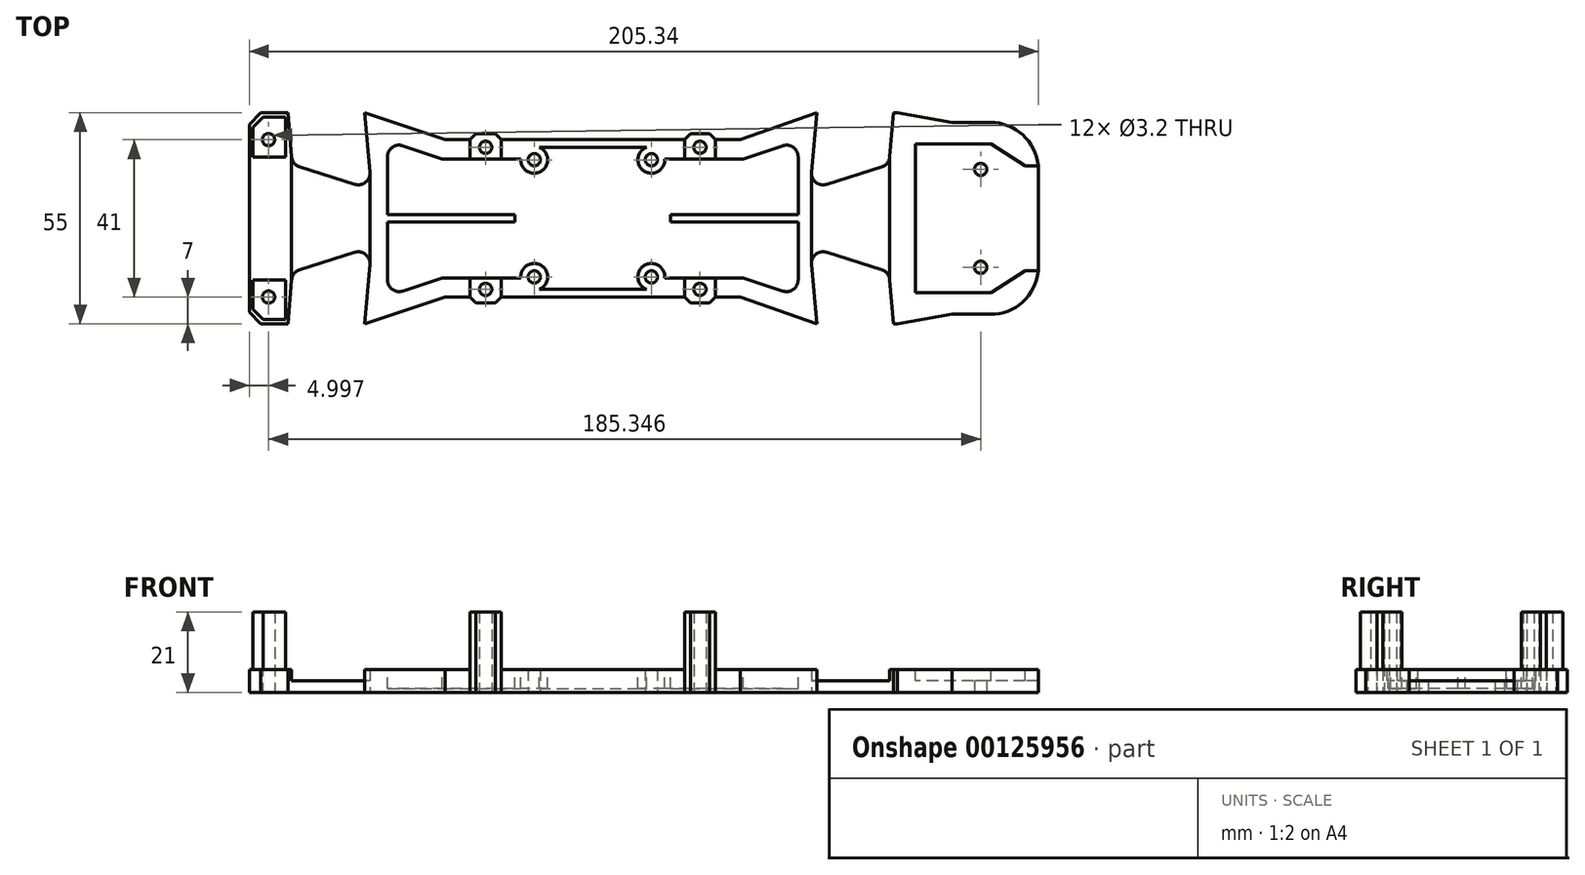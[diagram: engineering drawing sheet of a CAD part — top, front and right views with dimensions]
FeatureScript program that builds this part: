
annotation { "Feature Type Name" : "Feature", "Feature Type Description" : "" }
export const myFeature = defineFeature(function(context is Context, id is Id, definition is map)
    precondition{}
    {
        {
            var Q0;
            Q0=qCreatedBy(makeId("Top.planeOp"),FACE);
            var sketch = newSketch(context, id + "F0", { "sketchPlane" : qUnion([Q0])});
            skLineSegment(sketch, "E0", {"start": v(17.13, -22) * mm, "end": v(18.63, -20.5) * mm});
            skLineSegment(sketch, "E1", {"start": v(66.03, -27.5) * mm, "end": v(80.23, -25) * mm});
            skLineSegment(sketch, "E2", {"start": v(14.63, -22) * mm, "end": v(17.13, -22) * mm});
            skArc(sketch, "E3", {"start": v(90.23, -25) * mm, "mid": v(98.63, -21.75) * mm, "end": v(102.67, -13.7) * mm});
            skLineSegment(sketch, "E4", {"start": v(-102.67, 24.5) * mm, "end": v(-102.67, -24.5) * mm});
            skLineSegment(sketch, "E5", {"start": v(-51.67, -20.5) * mm, "end": v(-45.17, -20.5) * mm});
            skLineSegment(sketch, "E6", {"start": v(12.13, -22) * mm, "end": v(10.63, -20.5) * mm});
            skLineSegment(sketch, "E7", {"start": v(14.63, -22) * mm, "end": v(12.13, -22) * mm});
            skLineSegment(sketch, "E8", {"start": v(-43.67, -22) * mm, "end": v(-38.67, -22) * mm});
            skLineSegment(sketch, "E9", {"start": v(-43.67, -22) * mm, "end": v(-45.17, -20.5) * mm});
            skLineSegment(sketch, "E10", {"start": v(25.13, -20.5) * mm, "end": v(45.03, -27.5) * mm});
            skLineSegment(sketch, "E11", {"start": v(80.23, -25) * mm, "end": v(90.23, -25) * mm});
            skCircle(sketch, "E12", {"center": v(1.98, -15.25) * mm, "radius": 1.6 * mm});
            skCircle(sketch, "E13", {"center": v(-28.52, -15.25) * mm, "radius": 1.6 * mm});
            skLineSegment(sketch, "E14", {"start": v(18.63, -20.5) * mm, "end": v(25.13, -20.5) * mm});
            skCircle(sketch, "E15", {"center": v(87.67, -12.75) * mm, "radius": 1.6 * mm});
            skLineSegment(sketch, "E16", {"start": v(-37.17, -20.5) * mm, "end": v(10.63, -20.5) * mm});
            skLineSegment(sketch, "E17", {"start": v(-72.67, -27.5) * mm, "end": v(-51.67, -20.5) * mm});
            skLineSegment(sketch, "E18", {"start": v(102.67, 13.7) * mm, "end": v(102.67, -13.7) * mm});
            skLineSegment(sketch, "E19", {"start": v(-41.17, -22) * mm, "end": v(-43.67, -22) * mm});
            skLineSegment(sketch, "E20", {"start": v(-38.67, -22) * mm, "end": v(-37.17, -20.5) * mm});
            skLineSegment(sketch, "E21", {"start": v(-99.67, -27.5) * mm, "end": v(-92.67, -27.5) * mm});
            skLineSegment(sketch, "E22", {"start": v(-31.87, 0) * mm, "end": v(-19.1, 0) * mm, "construction": true});
            skLineSegment(sketch, "E23", {"start": v(-13.82, -38.87) * mm, "end": v(-13.82, -45.04) * mm, "construction": true});
            skLineSegment(sketch, "E24", {"start": v(65.02, -27.5) * mm, "end": v(66.03, -27.5) * mm});
            skLineSegment(sketch, "E25.MirrorCS", {"start": v(-43.67, 22) * mm, "end": v(-45.17, 20.5) * mm});
            skLineSegment(sketch, "E26.MirrorCS", {"start": v(-38.67, 22) * mm, "end": v(-37.17, 20.5) * mm});
            skLineSegment(sketch, "E27.MirrorCS", {"start": v(12.13, 22) * mm, "end": v(10.63, 20.5) * mm});
            skLineSegment(sketch, "E28.MirrorCS", {"start": v(14.63, 22) * mm, "end": v(12.13, 22) * mm});
            skLineSegment(sketch, "E29.MirrorCS", {"start": v(65.02, 27.5) * mm, "end": v(66.03, 27.5) * mm});
            skLineSegment(sketch, "E30.MirrorCS", {"start": v(17.13, 22) * mm, "end": v(18.63, 20.5) * mm});
            skLineSegment(sketch, "E31.MirrorCS", {"start": v(14.63, 22) * mm, "end": v(17.13, 22) * mm});
            skLineSegment(sketch, "E32.MirrorCS", {"start": v(-43.67, 22) * mm, "end": v(-38.67, 22) * mm});
            skCircle(sketch, "E33.MirrorC", {"center": v(87.67, 12.75) * mm, "radius": 1.6 * mm});
            skLineSegment(sketch, "E34.MirrorCS", {"start": v(25.13, 20.5) * mm, "end": v(45.03, 27.5) * mm});
            skLineSegment(sketch, "E35.MirrorCS", {"start": v(66.03, 27.5) * mm, "end": v(80.23, 25) * mm});
            skArc(sketch, "E36.MirrorCS", {"start": v(90.23, 25) * mm, "mid": v(98.63, 21.75) * mm, "end": v(102.67, 13.7) * mm});
            skLineSegment(sketch, "E37.MirrorCS", {"start": v(-72.67, 27.5) * mm, "end": v(-51.67, 20.5) * mm});
            skLineSegment(sketch, "E38.MirrorCS", {"start": v(-99.67, 27.5) * mm, "end": v(-92.67, 27.5) * mm});
            skCircle(sketch, "E39.MirrorC", {"center": v(1.98, 15.25) * mm, "radius": 1.6 * mm});
            skLineSegment(sketch, "E40.MirrorCS", {"start": v(-51.67, 20.5) * mm, "end": v(-45.17, 20.5) * mm});
            skCircle(sketch, "E41.MirrorC", {"center": v(-28.52, 15.25) * mm, "radius": 1.6 * mm});
            skLineSegment(sketch, "E42.MirrorCS", {"start": v(-37.17, 20.5) * mm, "end": v(10.63, 20.5) * mm});
            skLineSegment(sketch, "E43.MirrorCS", {"start": v(18.63, 20.5) * mm, "end": v(25.13, 20.5) * mm});
            skLineSegment(sketch, "E44.MirrorCS", {"start": v(80.23, 25) * mm, "end": v(90.23, 25) * mm});
            skCircle(sketch, "E45", {"center": v(-97.67, 20.5) * mm, "radius": 1.6 * mm});
            skCircle(sketch, "E46", {"center": v(-97.67, -20.5) * mm, "radius": 1.6 * mm});
            skLineSegment(sketch, "E47", {"start": v(-99.67, 27.5) * mm, "end": v(-102.67, 24.5) * mm});
            skLineSegment(sketch, "E48", {"start": v(-99.67, -27.5) * mm, "end": v(-102.67, -24.5) * mm});
            skLineSegment(sketch, "E49", {"start": v(-92.67, -27.5) * mm, "end": v(-91.67, -16) * mm});
            skLineSegment(sketch, "E50", {"start": v(-72.67, -27.5) * mm, "end": v(-71.31, -11.98) * mm});
            skLineSegment(sketch, "E51", {"start": v(-89.58, -13.4) * mm, "end": v(-75.2, -8.85) * mm});
            skPoint(sketch, "E52.visualSharp", {"position": v(-91.5, -14) * mm});
            skArc(sketch, "E52.filletArc", {"start": v(-89.58, -13.4) * mm, "mid": v(-91.02, -14.38) * mm, "end": v(-91.67, -16) * mm});
            skPoint(sketch, "E53.visualSharp", {"position": v(-70.92, -7.5) * mm});
            skArc(sketch, "E53.filletArc", {"start": v(-71.31, -11.98) * mm, "mid": v(-72.43, -9.37) * mm, "end": v(-75.2, -8.85) * mm});
            skLineSegment(sketch, "E54.MirrorCS", {"start": v(65.02, -27.5) * mm, "end": v(64.02, -16) * mm});
            skArc(sketch, "E55.MirrorCS", {"start": v(61.93, -13.4) * mm, "mid": v(63.37, -14.38) * mm, "end": v(64.02, -16) * mm});
            skLineSegment(sketch, "E56.MirrorCS", {"start": v(61.93, -13.4) * mm, "end": v(47.56, -8.85) * mm});
            skArc(sketch, "E57.MirrorCS", {"start": v(43.67, -11.98) * mm, "mid": v(44.78, -9.37) * mm, "end": v(47.56, -8.85) * mm});
            skLineSegment(sketch, "E58.MirrorCS", {"start": v(45.02, -27.5) * mm, "end": v(43.67, -11.98) * mm});
            skLineSegment(sketch, "E59.MirrorCS", {"start": v(-92.67, 27.5) * mm, "end": v(-91.67, 16) * mm});
            skPoint(sketch, "E60.MirrorP", {"position": v(-91.5, 14) * mm});
            skArc(sketch, "E61.MirrorCS", {"start": v(-89.58, 13.4) * mm, "mid": v(-91.02, 14.38) * mm, "end": v(-91.67, 16) * mm});
            skLineSegment(sketch, "E62.MirrorCS", {"start": v(-89.58, 13.4) * mm, "end": v(-75.2, 8.85) * mm});
            skArc(sketch, "E63.MirrorCS", {"start": v(-71.31, 11.98) * mm, "mid": v(-72.43, 9.37) * mm, "end": v(-75.2, 8.85) * mm});
            skLineSegment(sketch, "E64.MirrorCS", {"start": v(-72.67, 27.5) * mm, "end": v(-71.31, 11.98) * mm});
            skLineSegment(sketch, "E65.MirrorCS", {"start": v(65.02, 27.5) * mm, "end": v(64.02, 16) * mm});
            skArc(sketch, "E66.MirrorCS", {"start": v(61.93, 13.4) * mm, "mid": v(63.37, 14.38) * mm, "end": v(64.02, 16) * mm});
            skLineSegment(sketch, "E67.MirrorCS", {"start": v(61.93, 13.4) * mm, "end": v(47.56, 8.85) * mm});
            skArc(sketch, "E68.MirrorCS", {"start": v(43.67, 11.98) * mm, "mid": v(44.78, 9.37) * mm, "end": v(47.56, 8.85) * mm});
            skLineSegment(sketch, "E69.MirrorCS", {"start": v(45.02, 27.5) * mm, "end": v(43.67, 11.98) * mm});
            skCircle(sketch, "E70", {"center": v(-41.17, 18.5) * mm, "radius": 1.6 * mm});
            skCircle(sketch, "E71.MirrorC", {"center": v(-41.17, -18.5) * mm, "radius": 1.6 * mm});
            skLineSegment(sketch, "E72", {"start": v(-13.27, -11.98) * mm, "end": v(-13.27, -8.87) * mm, "construction": true});
            skCircle(sketch, "E73.MirrorC", {"center": v(14.63, -18.5) * mm, "radius": 1.6 * mm});
            skCircle(sketch, "E74.MirrorC", {"center": v(14.63, 18.5) * mm, "radius": 1.6 * mm});
            skSolve(sketch);
        }
        {
            var Q0;
            Q0=makeQuery(id+"F0.imprint","IMPRINT",FACE,{"disambiguationData":[TD([[makeQuery(id+"F0.imprint","IMPRINT",EDGE,{"derivedFrom":sQuery(id+"F0.wireOp",EDGE,"E0")}),1.0]])]});
            extrude(context, id + "F1", {"entities" : qUnion([Q0]), "depth" : 3 * mm});
        }
        {
            var Q0;
            Q0=makeQuery(id+"F1.opExtrude","CAP_FACE",FACE,{"disambiguationData":[OSD([sQuery(id+"F0.wireOp",EDGE,"E0"),sQuery(id+"F0.wireOp",EDGE,"E1"),sQuery(id+"F0.wireOp",EDGE,"E2"),sQuery(id+"F0.wireOp",EDGE,"E3"),sQuery(id+"F0.wireOp",EDGE,"E4"),sQuery(id+"F0.wireOp",EDGE,"E5"),sQuery(id+"F0.wireOp",EDGE,"E6"),sQuery(id+"F0.wireOp",EDGE,"E7"),sQuery(id+"F0.wireOp",EDGE,"E8"),sQuery(id+"F0.wireOp",EDGE,"E9"),sQuery(id+"F0.wireOp",EDGE,"E10"),sQuery(id+"F0.wireOp",EDGE,"E11"),sQuery(id+"F0.wireOp",EDGE,"E12"),sQuery(id+"F0.wireOp",EDGE,"E13"),sQuery(id+"F0.wireOp",EDGE,"E14"),sQuery(id+"F0.wireOp",EDGE,"E15"),sQuery(id+"F0.wireOp",EDGE,"E16"),sQuery(id+"F0.wireOp",EDGE,"E17"),sQuery(id+"F0.wireOp",EDGE,"E18"),sQuery(id+"F0.wireOp",EDGE,"E19"),sQuery(id+"F0.wireOp",EDGE,"cacf1cef-0e85-476d-93d9-f38397325373"),sQuery(id+"F0.wireOp",EDGE,"E20"),sQuery(id+"F0.wireOp",EDGE,"E21"),sQuery(id+"F0.wireOp",EDGE,"ktilFzmr-dvzl-N5Si-9QJE-yYhrjEpCdq7n"),sQuery(id+"F0.wireOp",EDGE,"E24"),sQuery(id+"F0.wireOp",EDGE,"y4Y6HD6z-qHML-mSbB-IgaJ-mIwfbL7wUbv0"),sQuery(id+"F0.wireOp",EDGE,"iBA37CV8-DKIr-jiMQ-xKjg-X3JWPwUv4cM2"),sQuery(id+"F0.wireOp",EDGE,"d3470dd5-383c-460f-b080-c6315553abd8.filletArc"),sQuery(id+"F0.wireOp",EDGE,"3242f57e-5447-41c4-bb9e-3e6edaabaf53.filletArc"),sQuery(id+"F0.wireOp",EDGE,"8b0b9065-8131-4a12-877d-2f3f4031bb290.MirrorCS"),sQuery(id+"F0.wireOp",EDGE,"cd60102b-e517-490f-9958-59f3726d56970.MirrorCS"),sQuery(id+"F0.wireOp",EDGE,"a92283b3-0195-4067-93ac-9b1154ab97d00.MirrorCS"),sQuery(id+"F0.wireOp",EDGE,"be52c130-8e04-43e8-8735-bc38e122cce20.MirrorCS"),sQuery(id+"F0.wireOp",EDGE,"8f306e8a-6cf5-47b0-af38-d5a049e91b220.MirrorCS"),sQuery(id+"F0.wireOp",EDGE,"E25.MirrorCS"),sQuery(id+"F0.wireOp",EDGE,"E26.MirrorCS"),sQuery(id+"F0.wireOp",EDGE,"E27.MirrorCS"),sQuery(id+"F0.wireOp",EDGE,"E28.MirrorCS"),sQuery(id+"F0.wireOp",EDGE,"E29.MirrorCS"),sQuery(id+"F0.wireOp",EDGE,"0e7726c4-7c47-45c0-a996-f9083ab80f9b5.MirrorCS"),sQuery(id+"F0.wireOp",EDGE,"E30.MirrorCS"),sQuery(id+"F0.wireOp",EDGE,"E31.MirrorCS"),sQuery(id+"F0.wireOp",EDGE,"E32.MirrorCS"),sQuery(id+"F0.wireOp",EDGE,"0e7726c4-7c47-45c0-a996-f9083ab80f9b9.MirrorCS"),sQuery(id+"F0.wireOp",EDGE,"E260.MirrorCS"),sQuery(id+"F0.wireOp",EDGE,"E33.MirrorC"),sQuery(id+"F0.wireOp",EDGE,"E262.MirrorCS"),sQuery(id+"F0.wireOp",EDGE,"E263.MirrorCS"),sQuery(id+"F0.wireOp",EDGE,"E34.MirrorCS"),sQuery(id+"F0.wireOp",EDGE,"E265.MirrorCS"),sQuery(id+"F0.wireOp",EDGE,"E266.MirrorCS"),sQuery(id+"F0.wireOp",EDGE,"E35.MirrorCS"),sQuery(id+"F0.wireOp",EDGE,"E36.MirrorCS"),sQuery(id+"F0.wireOp",EDGE,"E37.MirrorCS"),sQuery(id+"F0.wireOp",EDGE,"E270.MirrorCS"),sQuery(id+"F0.wireOp",EDGE,"E271.MirrorCS"),sQuery(id+"F0.wireOp",EDGE,"E273.MirrorCS"),sQuery(id+"F0.wireOp",EDGE,"E38.MirrorCS"),sQuery(id+"F0.wireOp",EDGE,"E39.MirrorC"),sQuery(id+"F0.wireOp",EDGE,"E40.MirrorCS"),sQuery(id+"F0.wireOp",EDGE,"E278.MirrorCS"),sQuery(id+"F0.wireOp",EDGE,"E41.MirrorC"),sQuery(id+"F0.wireOp",EDGE,"E280.MirrorCS"),sQuery(id+"F0.wireOp",EDGE,"E42.MirrorCS"),sQuery(id+"F0.wireOp",EDGE,"E43.MirrorCS"),sQuery(id+"F0.wireOp",EDGE,"E44.MirrorCS")])],"isStart":false});
            var sketch = newSketch(context, id + "F2", { "sketchPlane" : qUnion([Q0])});
            skLineSegment(sketch, "E75", {"start": v(-91.67, 16.06) * mm, "end": v(-91.67, -16.06) * mm});
            skLineSegment(sketch, "E76", {"start": v(64.02, 16.06) * mm, "end": v(64.02, -16.06) * mm});
            skLineSegment(sketch, "E77", {"start": v(-71.31, 11.98) * mm, "end": v(-71.31, -11.98) * mm});
            skLineSegment(sketch, "E78", {"start": v(43.67, 11.98) * mm, "end": v(43.67, -11.98) * mm});
            skSolve(sketch);
        }
        {
            var Q0;
            {var subQ3=sQuery(id+"F2.wireOp",EDGE,"E75");Q0=makeQuery(id+"F2.imprint","IMPRINT",FACE,{"disambiguationData":[TD([[makeQuery(id+"F2.imprint","IMPRINT",EDGE,{"derivedFrom":subQ3}),-1.0]])]});}
            var Q1;
            Q1=makeQuery(id+"F2.imprint","IMPRINT",FACE,{"disambiguationData":[TD([[makeQuery(id+"F2.imprint","IMPRINT",EDGE,{"derivedFrom":makeQuery(id+"F1.opExtrude","CAP_EDGE",EDGE,{"disambiguationData":[OSD([sQuery(id+"F0.wireOp",EDGE,"E0")])],"isStart":false})}),1.0]])]});
            var Q2;
            {var subQ1=sQuery(id+"F2.wireOp",EDGE,"E76");Q2=makeQuery(id+"F2.imprint","IMPRINT",FACE,{"disambiguationData":[TD([[makeQuery(id+"F2.imprint","IMPRINT",EDGE,{"derivedFrom":subQ1}),1.0]])]});}
            extrude(context, id + "F3", {"entities" : qUnion([Q0, Q1, Q2]), "operationType" : NewBodyOperationType.ADD, "depth" : 3 * mm});
        }
        {
            var Q0;
            Q0=makeQuery(id+"F3.opExtrude","CAP_FACE",FACE,{"disambiguationData":[OSD([sQuery(id+"F0.wireOp",EDGE,"E0"),sQuery(id+"F0.wireOp",EDGE,"E2"),sQuery(id+"F0.wireOp",EDGE,"E5"),sQuery(id+"F0.wireOp",EDGE,"E6"),sQuery(id+"F0.wireOp",EDGE,"E7"),sQuery(id+"F0.wireOp",EDGE,"E8"),sQuery(id+"F0.wireOp",EDGE,"E9"),sQuery(id+"F0.wireOp",EDGE,"E10"),sQuery(id+"F0.wireOp",EDGE,"E12"),sQuery(id+"F0.wireOp",EDGE,"E13"),sQuery(id+"F0.wireOp",EDGE,"E14"),sQuery(id+"F0.wireOp",EDGE,"E16"),sQuery(id+"F0.wireOp",EDGE,"E17"),sQuery(id+"F0.wireOp",EDGE,"E19"),sQuery(id+"F0.wireOp",EDGE,"E20"),sQuery(id+"F0.wireOp",EDGE,"E25.MirrorCS"),sQuery(id+"F0.wireOp",EDGE,"E26.MirrorCS"),sQuery(id+"F0.wireOp",EDGE,"E27.MirrorCS"),sQuery(id+"F0.wireOp",EDGE,"E28.MirrorCS"),sQuery(id+"F0.wireOp",EDGE,"E30.MirrorCS"),sQuery(id+"F0.wireOp",EDGE,"E31.MirrorCS"),sQuery(id+"F0.wireOp",EDGE,"E32.MirrorCS"),sQuery(id+"F0.wireOp",EDGE,"0e7726c4-7c47-45c0-a996-f9083ab80f9b9.MirrorCS"),sQuery(id+"F0.wireOp",EDGE,"E34.MirrorCS"),sQuery(id+"F0.wireOp",EDGE,"E37.MirrorCS"),sQuery(id+"F0.wireOp",EDGE,"E39.MirrorC"),sQuery(id+"F0.wireOp",EDGE,"E40.MirrorCS"),sQuery(id+"F0.wireOp",EDGE,"E41.MirrorC"),sQuery(id+"F0.wireOp",EDGE,"E42.MirrorCS"),sQuery(id+"F0.wireOp",EDGE,"E43.MirrorCS"),sQuery(id+"F2.wireOp",EDGE,"XH4723qV-k9EK-rnyf-MCnd-NPgPMgAZq0qj"),sQuery(id+"F2.wireOp",EDGE,"VkoqZiKv-uEe6-g3Ky-yl9S-WlclnUHpSLVB"),sQuery(id+"F2.wireOp",EDGE,"4zoe9t7i-jXsD-BC2V-jVCx-dnIx5Sm0L1ok"),sQuery(id+"F2.wireOp",EDGE,"oUknClw5-JEGL-fXPA-mKYg-SWGIKpQydZco"),sQuery(id+"F2.wireOp",EDGE,"MJO4RlAT-fQuh-MutT-Yoxh-jH0xN2Fm8YoV"),sQuery(id+"F2.wireOp",EDGE,"r3oGAgAb-fgCM-ykX4-cEjS-qaDw403mrGcw")])],"isStart":false});
            var sketch = newSketch(context, id + "F4", { "sketchPlane" : qUnion([Q0])});
            skLineSegment(sketch, "E79", {"start": v(-62.77, 18.93) * mm, "end": v(-52.48, 15.5) * mm});
            skLineSegment(sketch, "E80", {"start": v(-52.48, 15.5) * mm, "end": v(-32.01, 15.5) * mm});
            skCircle(sketch, "E81", {"center": v(-28.52, 15.25) * mm, "radius": 3.5 * mm, "construction": true});
            skLineSegment(sketch, "E82", {"start": v(-8.2, 0) * mm, "end": v(-15.48, 0) * mm, "construction": true});
            skLineSegment(sketch, "E83", {"start": v(-13.27, -7.12) * mm, "end": v(-13.27, -2.95) * mm, "construction": true});
            skCircle(sketch, "E84", {"center": v(1.98, 15.25) * mm, "radius": 3.5 * mm, "construction": true});
            skLineSegment(sketch, "E85", {"start": v(-27.22, 18.5) * mm, "end": v(0.68, 18.5) * mm});
            skLineSegment(sketch, "E86.MirrorCS", {"start": v(25.94, 15.5) * mm, "end": v(5.47, 15.5) * mm});
            skLineSegment(sketch, "E87.MirrorCS", {"start": v(36.22, 18.93) * mm, "end": v(25.94, 15.5) * mm});
            skLineSegment(sketch, "E88.MirrorCS", {"start": v(-52.48, -15.5) * mm, "end": v(-32.01, -15.5) * mm});
            skLineSegment(sketch, "E89.MirrorCS", {"start": v(-62.77, -18.93) * mm, "end": v(-52.48, -15.5) * mm});
            skCircle(sketch, "E90.MirrorC", {"center": v(1.98, -15.25) * mm, "radius": 3.5 * mm, "construction": true});
            skCircle(sketch, "E91.MirrorC", {"center": v(-28.52, -15.25) * mm, "radius": 3.5 * mm, "construction": true});
            skLineSegment(sketch, "E92.MirrorCS", {"start": v(-27.22, -18.5) * mm, "end": v(0.68, -18.5) * mm});
            skLineSegment(sketch, "E93.MirrorCS", {"start": v(36.22, -18.93) * mm, "end": v(25.94, -15.5) * mm});
            skLineSegment(sketch, "E94.MirrorCS", {"start": v(25.94, -15.5) * mm, "end": v(5.47, -15.5) * mm});
            skLineSegment(sketch, "E95", {"start": v(-66.71, 16.08) * mm, "end": v(-66.71, -16.08) * mm});
            skLineSegment(sketch, "E96", {"start": v(40.17, 16.08) * mm, "end": v(40.17, -16.08) * mm});
            skPoint(sketch, "E97.visualSharp", {"position": v(-66.71, 20.24) * mm});
            skArc(sketch, "E97.filletArc", {"start": v(-62.77, 18.93) * mm, "mid": v(-65.47, 18.51) * mm, "end": v(-66.71, 16.08) * mm});
            skPoint(sketch, "E98.visualSharp", {"position": v(-66.71, -20.24) * mm});
            skArc(sketch, "E98.filletArc", {"start": v(-66.71, -16.08) * mm, "mid": v(-65.47, -18.51) * mm, "end": v(-62.77, -18.93) * mm});
            skPoint(sketch, "E99.visualSharp", {"position": v(40.17, 20.24) * mm});
            skArc(sketch, "E99.filletArc", {"start": v(40.17, 16.08) * mm, "mid": v(38.92, 18.51) * mm, "end": v(36.22, 18.93) * mm});
            skPoint(sketch, "E100.visualSharp", {"position": v(40.17, -20.24) * mm});
            skArc(sketch, "E100.filletArc", {"start": v(36.22, -18.93) * mm, "mid": v(38.92, -18.51) * mm, "end": v(40.17, -16.08) * mm});
            skLineSegment(sketch, "E101", {"start": v(-33.52, 1) * mm, "end": v(-66.71, 1) * mm});
            skLineSegment(sketch, "E102.MirrorCS", {"start": v(6.98, 1) * mm, "end": v(40.17, 1) * mm});
            skLineSegment(sketch, "E103.MirrorCS", {"start": v(-33.52, -1) * mm, "end": v(-66.71, -1) * mm});
            skLineSegment(sketch, "E104.MirrorCS", {"start": v(6.98, -1) * mm, "end": v(40.17, -1) * mm});
            skLineSegment(sketch, "E105", {"start": v(-33.52, 1) * mm, "end": v(-33.52, -1) * mm});
            skLineSegment(sketch, "E106", {"start": v(6.98, 1) * mm, "end": v(6.98, -1) * mm});
            skArc(sketch, "E107", {"start": v(-32.01, -15.5) * mm, "mid": v(-26.67, -12.28) * mm, "end": v(-27.22, -18.5) * mm});
            skArc(sketch, "E108", {"start": v(0.68, -18.5) * mm, "mid": v(0.12, -12.28) * mm, "end": v(5.47, -15.5) * mm});
            skArc(sketch, "E109", {"start": v(5.47, 15.5) * mm, "mid": v(0.12, 12.28) * mm, "end": v(0.68, 18.5) * mm});
            skArc(sketch, "E110", {"start": v(-32.01, 15.5) * mm, "mid": v(-26.67, 12.28) * mm, "end": v(-27.22, 18.5) * mm});
            skSolve(sketch);
        }
        {
            var Q0;
            Q0=makeQuery(id+"F4.imprint","IMPRINT",FACE,{"disambiguationData":[TD([[makeQuery(id+"F4.imprint","IMPRINT",EDGE,{"derivedFrom":sQuery(id+"F4.wireOp",EDGE,"E79")}),-1.0]])]});
            extrude(context, id + "F5", {"entities" : qUnion([Q0]), "operationType" : NewBodyOperationType.REMOVE, "oppositeDirection" : true, "depth" : 5 * mm});
        }
        {
            var Q0;
            Q0=makeQuery(id+"F3.opExtrude","CAP_FACE",FACE,{"disambiguationData":[OSD([sQuery(id+"F0.wireOp",EDGE,"E4"),sQuery(id+"F0.wireOp",EDGE,"E21"),sQuery(id+"F0.wireOp",EDGE,"ktilFzmr-dvzl-N5Si-9QJE-yYhrjEpCdq7n"),sQuery(id+"F0.wireOp",EDGE,"E38.MirrorCS"),sQuery(id+"F0.wireOp",EDGE,"E280.MirrorCS"),sQuery(id+"F0.wireOp",EDGE,"E45"),sQuery(id+"F0.wireOp",EDGE,"E46"),sQuery(id+"F0.wireOp",EDGE,"E47"),sQuery(id+"F0.wireOp",EDGE,"E48"),sQuery(id+"F2.wireOp",EDGE,"E75")])],"isStart":false});
            var sketch = newSketch(context, id + "F6", { "sketchPlane" : qUnion([Q0])});
            skLineSegment(sketch, "E111", {"start": v(-93.19, -26.38) * mm, "end": v(-99.14, -26.38) * mm});
            skLineSegment(sketch, "E112", {"start": v(-99.14, -26.38) * mm, "end": v(-101.78, -23.73) * mm});
            skLineSegment(sketch, "E113", {"start": v(-101.78, -23.73) * mm, "end": v(-101.78, -16.01) * mm});
            skLineSegment(sketch, "E114", {"start": v(-101.78, -16.01) * mm, "end": v(-93.19, -16.01) * mm});
            skLineSegment(sketch, "E115", {"start": v(-93.19, -16.01) * mm, "end": v(-93.19, -26.38) * mm});
            skLineSegment(sketch, "E116", {"start": v(-94.05, 0) * mm, "end": v(-99.2, 0) * mm, "construction": true});
            skLineSegment(sketch, "E117.MirrorCS", {"start": v(-93.19, 16.01) * mm, "end": v(-93.19, 26.38) * mm});
            skLineSegment(sketch, "E118.MirrorCS", {"start": v(-101.78, 16.01) * mm, "end": v(-93.19, 16.01) * mm});
            skLineSegment(sketch, "E119.MirrorCS", {"start": v(-101.78, 23.73) * mm, "end": v(-101.78, 16.01) * mm});
            skLineSegment(sketch, "E120.MirrorCS", {"start": v(-99.14, 26.38) * mm, "end": v(-101.78, 23.73) * mm});
            skLineSegment(sketch, "E121.MirrorCS", {"start": v(-93.19, 26.38) * mm, "end": v(-99.14, 26.38) * mm});
            skSolve(sketch);
        }
        {
            var Q0;
            Q0=makeQuery(id+"F6.imprint","IMPRINT",FACE,{"disambiguationData":[TD([[makeQuery(id+"F6.imprint","IMPRINT",EDGE,{"derivedFrom":sQuery(id+"F6.wireOp",EDGE,"E117.MirrorCS")}),1.0]])]});
            var Q1;
            Q1=makeQuery(id+"F6.imprint","IMPRINT",FACE,{"disambiguationData":[TD([[makeQuery(id+"F6.imprint","IMPRINT",EDGE,{"derivedFrom":sQuery(id+"F6.wireOp",EDGE,"E111")}),-1.0]])]});
            extrude(context, id + "F7", {"entities" : qUnion([Q0, Q1]), "operationType" : NewBodyOperationType.ADD, "depth" : 15 * mm});
        }
        {
            var Q0;
            Q0=makeQuery(id+"F3.opExtrude","CAP_FACE",FACE,{"disambiguationData":[OSD([sQuery(id+"F0.wireOp",EDGE,"E0"),sQuery(id+"F0.wireOp",EDGE,"E2"),sQuery(id+"F0.wireOp",EDGE,"E5"),sQuery(id+"F0.wireOp",EDGE,"E6"),sQuery(id+"F0.wireOp",EDGE,"E7"),sQuery(id+"F0.wireOp",EDGE,"E8"),sQuery(id+"F0.wireOp",EDGE,"E9"),sQuery(id+"F0.wireOp",EDGE,"E10"),sQuery(id+"F0.wireOp",EDGE,"E12"),sQuery(id+"F0.wireOp",EDGE,"E13"),sQuery(id+"F0.wireOp",EDGE,"E14"),sQuery(id+"F0.wireOp",EDGE,"E16"),sQuery(id+"F0.wireOp",EDGE,"E17"),sQuery(id+"F0.wireOp",EDGE,"E19"),sQuery(id+"F0.wireOp",EDGE,"E20"),sQuery(id+"F0.wireOp",EDGE,"E25.MirrorCS"),sQuery(id+"F0.wireOp",EDGE,"E26.MirrorCS"),sQuery(id+"F0.wireOp",EDGE,"E27.MirrorCS"),sQuery(id+"F0.wireOp",EDGE,"E28.MirrorCS"),sQuery(id+"F0.wireOp",EDGE,"E30.MirrorCS"),sQuery(id+"F0.wireOp",EDGE,"E31.MirrorCS"),sQuery(id+"F0.wireOp",EDGE,"E32.MirrorCS"),sQuery(id+"F0.wireOp",EDGE,"0e7726c4-7c47-45c0-a996-f9083ab80f9b9.MirrorCS"),sQuery(id+"F0.wireOp",EDGE,"E34.MirrorCS"),sQuery(id+"F0.wireOp",EDGE,"E37.MirrorCS"),sQuery(id+"F0.wireOp",EDGE,"E39.MirrorC"),sQuery(id+"F0.wireOp",EDGE,"E40.MirrorCS"),sQuery(id+"F0.wireOp",EDGE,"E41.MirrorC"),sQuery(id+"F0.wireOp",EDGE,"E42.MirrorCS"),sQuery(id+"F0.wireOp",EDGE,"E43.MirrorCS"),sQuery(id+"F2.wireOp",EDGE,"XH4723qV-k9EK-rnyf-MCnd-NPgPMgAZq0qj"),sQuery(id+"F2.wireOp",EDGE,"VkoqZiKv-uEe6-g3Ky-yl9S-WlclnUHpSLVB"),sQuery(id+"F2.wireOp",EDGE,"4zoe9t7i-jXsD-BC2V-jVCx-dnIx5Sm0L1ok"),sQuery(id+"F2.wireOp",EDGE,"oUknClw5-JEGL-fXPA-mKYg-SWGIKpQydZco"),sQuery(id+"F2.wireOp",EDGE,"MJO4RlAT-fQuh-MutT-Yoxh-jH0xN2Fm8YoV"),sQuery(id+"F2.wireOp",EDGE,"r3oGAgAb-fgCM-ykX4-cEjS-qaDw403mrGcw")])],"isStart":false});
            var sketch = newSketch(context, id + "F8", { "sketchPlane" : qUnion([Q0])});
            skLineSegment(sketch, "E122", {"start": v(-37.17, -20.5) * mm, "end": v(-37.17, -15.5) * mm});
            skLineSegment(sketch, "E123", {"start": v(-45.17, -20.5) * mm, "end": v(-45.17, -15.5) * mm});
            skLineSegment(sketch, "E124", {"start": v(-8.39, 0) * mm, "end": v(-14.93, 0) * mm, "construction": true});
            skLineSegment(sketch, "E125", {"start": v(-13.27, -5.12) * mm, "end": v(-13.27, -1.7) * mm, "construction": true});
            skLineSegment(sketch, "E126.MirrorCS", {"start": v(-37.17, 20.5) * mm, "end": v(-37.17, 15.5) * mm});
            skLineSegment(sketch, "E127.MirrorCS", {"start": v(-45.17, 20.5) * mm, "end": v(-45.17, 15.5) * mm});
            skLineSegment(sketch, "E128.MirrorCS", {"start": v(10.63, -20.5) * mm, "end": v(10.63, -15.5) * mm});
            skLineSegment(sketch, "E129.MirrorCS", {"start": v(18.63, -20.5) * mm, "end": v(18.63, -15.5) * mm});
            skLineSegment(sketch, "E130.MirrorCS", {"start": v(10.63, 20.5) * mm, "end": v(10.63, 15.5) * mm});
            skLineSegment(sketch, "E131.MirrorCS", {"start": v(18.63, 20.5) * mm, "end": v(18.63, 15.5) * mm});
            skSolve(sketch);
        }
        {
            var Q0;
            {var subQ1=sQuery(id+"F8.wireOp",EDGE,"E126.MirrorCS");Q0=makeQuery(id+"F8.imprint","IMPRINT",FACE,{"disambiguationData":[TD([[makeQuery(id+"F8.imprint","IMPRINT",EDGE,{"derivedFrom":subQ1}),-1.0]])]});}
            var Q1;
            {var subQ1=sQuery(id+"F8.wireOp",EDGE,"E130.MirrorCS");Q1=makeQuery(id+"F8.imprint","IMPRINT",FACE,{"disambiguationData":[TD([[makeQuery(id+"F8.imprint","IMPRINT",EDGE,{"derivedFrom":subQ1}),1.0]])]});}
            var Q2;
            {var subQ1=sQuery(id+"F8.wireOp",EDGE,"E128.MirrorCS");Q2=makeQuery(id+"F8.imprint","IMPRINT",FACE,{"disambiguationData":[TD([[makeQuery(id+"F8.imprint","IMPRINT",EDGE,{"derivedFrom":subQ1}),-1.0]])]});}
            var Q3;
            {var subQ0=sQuery(id+"F8.wireOp",EDGE,"E122");Q3=makeQuery(id+"F8.imprint","IMPRINT",FACE,{"disambiguationData":[TD([[makeQuery(id+"F8.imprint","IMPRINT",EDGE,{"derivedFrom":subQ0}),1.0]])]});}
            extrude(context, id + "F9", {"entities" : qUnion([Q0, Q1, Q2, Q3]), "operationType" : NewBodyOperationType.ADD, "depth" : 15 * mm});
        }
        {
            var Q0;
            Q0=makeQuery(id+"F3.opExtrude","CAP_FACE",FACE,{"disambiguationData":[OSD([sQuery(id+"F0.wireOp",EDGE,"E1"),sQuery(id+"F0.wireOp",EDGE,"E3"),sQuery(id+"F0.wireOp",EDGE,"E11"),sQuery(id+"F0.wireOp",EDGE,"E15"),sQuery(id+"F0.wireOp",EDGE,"E18"),sQuery(id+"F0.wireOp",EDGE,"E24"),sQuery(id+"F0.wireOp",EDGE,"E29.MirrorCS"),sQuery(id+"F0.wireOp",EDGE,"E33.MirrorC"),sQuery(id+"F0.wireOp",EDGE,"E35.MirrorCS"),sQuery(id+"F0.wireOp",EDGE,"E36.MirrorCS"),sQuery(id+"F0.wireOp",EDGE,"E44.MirrorCS"),sQuery(id+"F0.wireOp",EDGE,"E54.MirrorCS"),sQuery(id+"F0.wireOp",EDGE,"E65.MirrorCS"),sQuery(id+"F2.wireOp",EDGE,"E76")])],"isStart":false});
            var sketch = newSketch(context, id + "F10", { "sketchPlane" : qUnion([Q0])});
            skLineSegment(sketch, "E132", {"start": v(102.67, -13.7) * mm, "end": v(99.29, -13.7) * mm});
            skLineSegment(sketch, "E133", {"start": v(99.29, -13.7) * mm, "end": v(90.44, -19.35) * mm});
            skLineSegment(sketch, "E134", {"start": v(90.44, -19.35) * mm, "end": v(70.67, -19.35) * mm});
            skLineSegment(sketch, "E135", {"start": v(79.72, 0) * mm, "end": v(89.47, 0) * mm, "construction": true});
            skPoint(sketch, "E135.endSnap0", {"position": v(64.02, 0) * mm});
            skLineSegment(sketch, "E136.MirrorCS", {"start": v(90.44, 19.35) * mm, "end": v(70.67, 19.35) * mm});
            skLineSegment(sketch, "E137.MirrorCS", {"start": v(99.29, 13.7) * mm, "end": v(90.44, 19.35) * mm});
            skLineSegment(sketch, "E138.MirrorCS", {"start": v(102.67, 13.7) * mm, "end": v(99.29, 13.7) * mm});
            skLineSegment(sketch, "E139", {"start": v(70.67, 19.35) * mm, "end": v(70.67, -19.35) * mm});
            skSolve(sketch);
        }
        {
            var Q0;
            Q0=makeQuery(id+"F10.imprint","IMPRINT",FACE,{"disambiguationData":[TD([[makeQuery(id+"F10.imprint","IMPRINT",EDGE,{"derivedFrom":sQuery(id+"F10.wireOp",EDGE,"E132")}),-1.0]])]});
            extrude(context, id + "F11", {"entities" : qUnion([Q0]), "operationType" : NewBodyOperationType.REMOVE, "oppositeDirection" : true, "depth" : 3 * mm});
        }
    });
